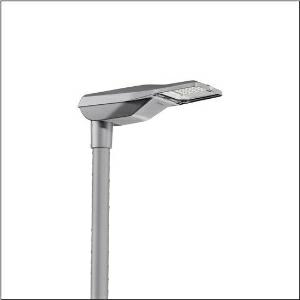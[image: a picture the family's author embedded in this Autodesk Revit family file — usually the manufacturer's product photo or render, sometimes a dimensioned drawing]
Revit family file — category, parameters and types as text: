
# Revit family: streetlight_sl_21_iq_micro___stw1_0a_5xe1e21d08cb_e74e
name_source: partatom
category: Lighting Fixtures
units: mm (PartAtom-declared; Revit-internal decimal feet)

## family parameters
Cut with Voids When Loaded = No
Host = Face
Light Source = No
Part Type = Normal
Room Calculation Point = No
Round Connector Dimension = Use Diameter
Shared = No

## types (1)
- --- (1 x LED, 2380 lm, 19.4 W, 2200K)
    Apparent Load = 19 VA
    CIE Flux Codes = 38 75 98 100 100
    Color Rendering = 70
    Color Temperature = 2200K
    Default Elevation = 1800 mm
    Description = Streetlight SL 21 iQ micro, mast luminaire, primary light control with lens, of PMMA, primary optical cover: cover, of toughened safety glass, transparent, light distribution: STW1.0a, light emission: direct distribution, primary light characteristic: asymmetric, installation type: post-top, side-entry, LED, High Power LED, rated luminous flux: 2.380lm, luminous efficacy: 123lm/W, light colour: 722, colour temperature: 2200K, control gear: iQ-Comfort, control: Auto-Match, Temp-Guard, Lumen-Switch, Night-Set, Smart-Wire, Light-Fading, Desk-Remote (wireless, voltage-free reading and setting of iQ features in the workshop via application-optimized NFC function/RFID function), optimised constant luminous flux control (CLO 2.0), pre-setting: linear dimming characteristic, mains connection: 220..240V, AC, 50/60Hz, start of lifetime: 19W, end of service life: 20W, reduction: 10W, luminaire housing, of diecast aluminium, powder-coated, SITECO metallic grey (DB 702S), corrosivity category C5 high according to DIN EN ISO 12944, please order mast flange separately, inclination adjustable: 0°, 5°, 10°, 15°, sealing non-destructively replaceable, multi-level sealing system, length: 528mm, width: 235mm, height: 110mm, mast flange for spigot size: 42mm (side-entry): 5XC10008XM4, 60/48mm (side-entry/post-top): 5XC10108XM2, 76/60mm (side-entry/post-top): 5XC10108XM1, protection rating (complete): IP66, insulation class (complete): insulation class II (safety insulation), certification: CE, ENEC, ENEC+, VDE, impact resistance: IK10, permissible operating ambient temperature for outdoor applications: -40..+50°C, standard-compliant lighting for roads and squares, packaging unit: 1 piece

Light Distribution: STW1.0a
    Height = 110 mm
    Lamp = 1 x LED
    Lamp Light Flux = 2380 lm
    Lamp Power = 19.4 W
    Lamp count = 1
    Length = 528 mm
    Luminous efficacy = 123 lm/W
    Manufacturer = Siteco
    ModVariant = No
    Model = 5XE1E21D08CB
    Number of Poles = 1
    OnlyDefault = Yes
    Power Factor = 1
    Product Name = Streetlight SL 21 iQ micro | STW1.0a
    Product group = mast luminaire | pylon top
    ProductGroupID = 6100
    Protection Class = Protection class II
    Protection Degree = IP 66
    RLX_Detail_Level = 1
    RLX_Emergency_Light_Flux = 0 lm
    RLX_Emergency_Type = 0
    RLX_Emergency_Type_DB = No
    RlxData = <blob elided: 98681 chars, md5=28c6dbbd>
    Socket = socket
    Standby Power = 0 W
    System Light Flux = 2380 lm
    System Power = 19 W
    Type Comments = factory setting: luminous flux: 100 % | dim-lin: 254 | 387 mA
    Type Image = l_1006881.jpg
    URL = http://relux.com
    VarID = @adj_138463
    Voltage = 0 V
    Weight = 0.00 kg
    Width = 235 mm

## geometry (parser evidence)
native form markers: Blend x4, Sweep x9
no freeform markers — native parametric forms only
